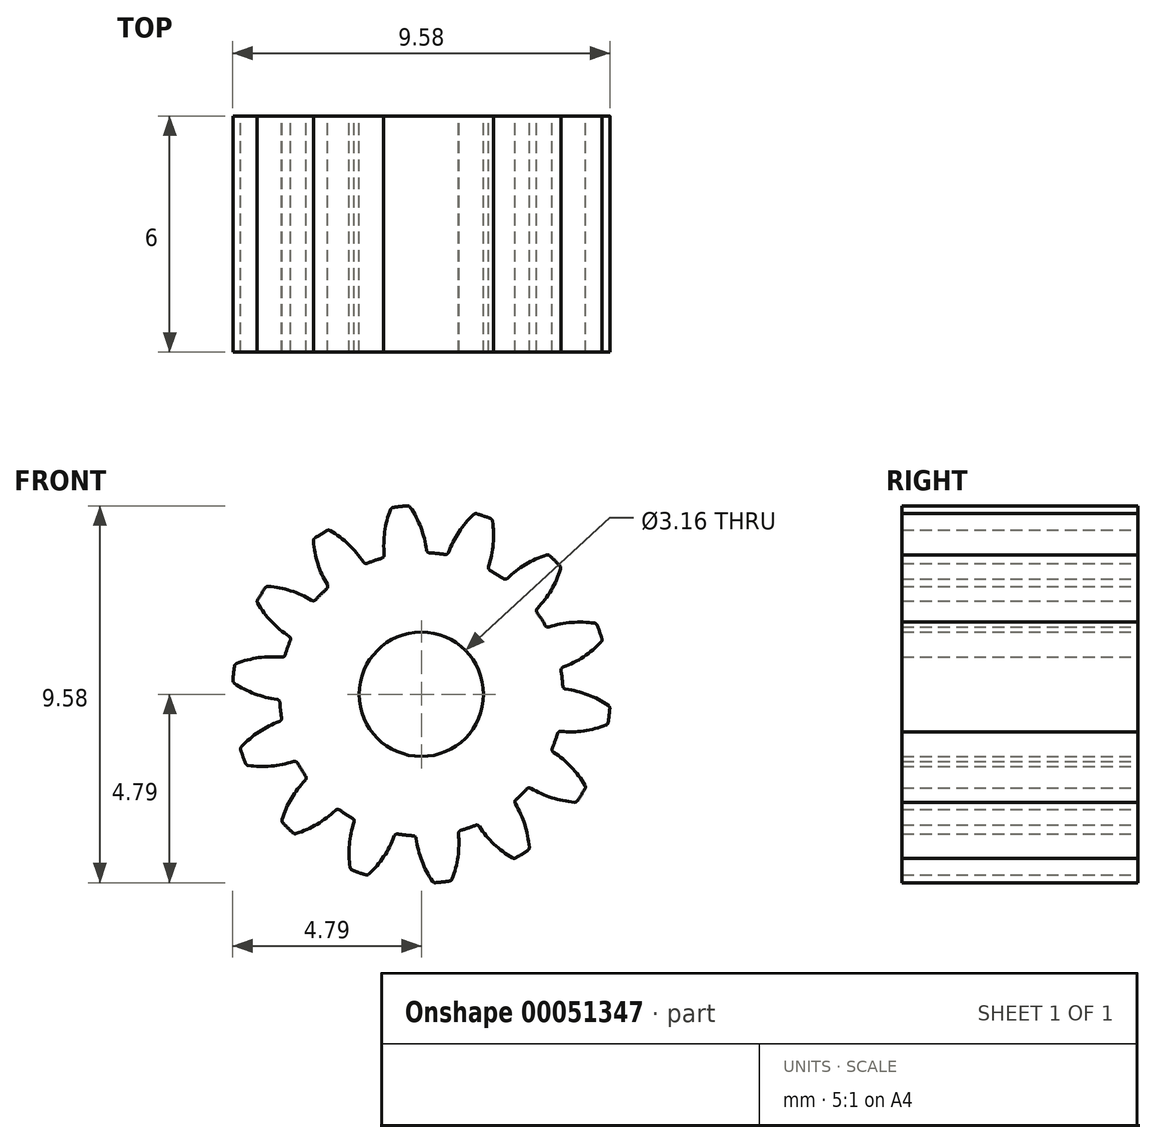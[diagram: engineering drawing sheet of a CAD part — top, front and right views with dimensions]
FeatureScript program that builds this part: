
annotation { "Feature Type Name" : "Feature", "Feature Type Description" : "" }
export const myFeature = defineFeature(function(context is Context, id is Id, definition is map)
    precondition{}
    {
        {
            var Q0;
            Q0=qCreatedBy(makeId("Front.planeOp"),FACE);
            var sketch = newSketch(context, id + "F0", { "sketchPlane" : qUnion([Q0])});
            skCircle(sketch, "E0", {"center": v(0, 0) * mm, "radius": 3.6 * mm, "construction": true});
            skCircle(sketch, "E1", {"center": v(0, 0) * mm, "radius": 4.2 * mm, "construction": true});
            skCircle(sketch, "E2", {"center": v(0, 0) * mm, "radius": 4.8 * mm, "construction": true});
            skLineSegment(sketch, "E3", {"start": v(0, 5.34) * mm, "end": v(0, -5.6) * mm, "construction": true});
            skLineSegment(sketch, "E4", {"start": v(0, 0) * mm, "end": v(-0.7, 6.23) * mm, "construction": true});
            skLineSegment(sketch, "E5", {"start": v(0, 4.2) * mm, "end": v(-5.98, 4.2) * mm, "construction": true});
            skLineSegment(sketch, "E6", {"start": v(0, 4.2) * mm, "end": v(-6, 2.02) * mm, "construction": true});
            skCircle(sketch, "E7", {"center": v(0, 4.2) * mm, "radius": 2.52 * mm, "construction": true});
            skPoint(sketch, "E8", {"position": v(-2.37, 3.34) * mm});
            skCircle(sketch, "E9", {"center": v(-2.37, 3.34) * mm, "radius": 2.52 * mm, "construction": true});
            skArc(sketch, "E10", {"start": v(0.13, 3.67) * mm, "mid": v(-0.01, 4.23) * mm, "end": v(-0.28, 4.75) * mm});
            skArc(sketch, "E11.MirrorCS", {"start": v(-0.94, 3.55) * mm, "mid": v(-0.93, 4.13) * mm, "end": v(-0.78, 4.7) * mm});
            skArc(sketch, "E12", {"start": v(-0.36, 4.79) * mm, "mid": v(-0.54, 4.77) * mm, "end": v(-0.72, 4.75) * mm});
            skArc(sketch, "E13", {"start": v(0.2, 3.6) * mm, "mid": v(0.4, -3.58) * mm, "end": v(-1, 3.46) * mm});
            skPoint(sketch, "E14.visualSharp", {"position": v(-0.94, 3.48) * mm});
            skArc(sketch, "E14.filletArc", {"start": v(-1, 3.46) * mm, "mid": v(-0.96, 3.5) * mm, "end": v(-0.94, 3.55) * mm});
            skPoint(sketch, "E15.visualSharp", {"position": v(0.14, 3.6) * mm});
            skArc(sketch, "E15.filletArc", {"start": v(0.13, 3.67) * mm, "mid": v(0.16, 3.62) * mm, "end": v(0.2, 3.6) * mm});
            skPoint(sketch, "E16.visualSharp", {"position": v(-0.3, 4.8) * mm});
            skArc(sketch, "E16.filletArc", {"start": v(-0.28, 4.75) * mm, "mid": v(-0.31, 4.78) * mm, "end": v(-0.36, 4.79) * mm});
            skPoint(sketch, "E17.visualSharp", {"position": v(-0.77, 4.74) * mm});
            skArc(sketch, "E17.filletArc", {"start": v(-0.72, 4.75) * mm, "mid": v(-0.76, 4.73) * mm, "end": v(-0.78, 4.7) * mm});
            skArc(sketch, "E18.1.0", {"start": v(-2.4, 2.68) * mm, "mid": v(-2.38, 2.73) * mm, "end": v(-2.39, 2.79) * mm});
            skArc(sketch, "E18.1.1", {"start": v(-2.39, 2.79) * mm, "mid": v(-2.63, 3.32) * mm, "end": v(-2.74, 3.89) * mm});
            skArc(sketch, "E18.1.2", {"start": v(-2.7, 3.96) * mm, "mid": v(-2.73, 3.93) * mm, "end": v(-2.74, 3.89) * mm});
            skArc(sketch, "E18.1.3", {"start": v(-2.4, 4.16) * mm, "mid": v(-2.55, 4.06) * mm, "end": v(-2.7, 3.96) * mm});
            skArc(sketch, "E18.1.4", {"start": v(-2.31, 4.16) * mm, "mid": v(-2.36, 4.17) * mm, "end": v(-2.4, 4.16) * mm});
            skArc(sketch, "E18.1.5", {"start": v(-1.47, 3.36) * mm, "mid": v(-1.85, 3.8) * mm, "end": v(-2.31, 4.16) * mm});
            skArc(sketch, "E18.1.6", {"start": v(-1.47, 3.36) * mm, "mid": v(-1.43, 3.33) * mm, "end": v(-1.37, 3.33) * mm});
            skArc(sketch, "E18.2.0", {"start": v(-3.33, 1.37) * mm, "mid": v(-3.33, 1.43) * mm, "end": v(-3.36, 1.47) * mm});
            skArc(sketch, "E18.2.1", {"start": v(-3.36, 1.47) * mm, "mid": v(-3.8, 1.85) * mm, "end": v(-4.16, 2.31) * mm});
            skArc(sketch, "E18.2.2", {"start": v(-4.16, 2.4) * mm, "mid": v(-4.17, 2.36) * mm, "end": v(-4.16, 2.31) * mm});
            skArc(sketch, "E18.2.3", {"start": v(-3.96, 2.7) * mm, "mid": v(-4.06, 2.55) * mm, "end": v(-4.16, 2.4) * mm});
            skArc(sketch, "E18.2.4", {"start": v(-3.89, 2.74) * mm, "mid": v(-3.93, 2.73) * mm, "end": v(-3.96, 2.7) * mm});
            skArc(sketch, "E18.2.5", {"start": v(-2.79, 2.39) * mm, "mid": v(-3.32, 2.63) * mm, "end": v(-3.89, 2.74) * mm});
            skArc(sketch, "E18.2.6", {"start": v(-2.79, 2.39) * mm, "mid": v(-2.73, 2.38) * mm, "end": v(-2.68, 2.4) * mm});
            skArc(sketch, "E18.3.0", {"start": v(-3.6, -0.2) * mm, "mid": v(-3.62, -0.16) * mm, "end": v(-3.67, -0.13) * mm});
            skArc(sketch, "E18.3.1", {"start": v(-3.67, -0.13) * mm, "mid": v(-4.23, 0.01) * mm, "end": v(-4.75, 0.28) * mm});
            skArc(sketch, "E18.3.2", {"start": v(-4.79, 0.36) * mm, "mid": v(-4.78, 0.31) * mm, "end": v(-4.75, 0.28) * mm});
            skArc(sketch, "E18.3.3", {"start": v(-4.75, 0.72) * mm, "mid": v(-4.77, 0.54) * mm, "end": v(-4.79, 0.36) * mm});
            skArc(sketch, "E18.3.4", {"start": v(-4.7, 0.78) * mm, "mid": v(-4.73, 0.76) * mm, "end": v(-4.75, 0.72) * mm});
            skArc(sketch, "E18.3.5", {"start": v(-3.55, 0.94) * mm, "mid": v(-4.13, 0.93) * mm, "end": v(-4.7, 0.78) * mm});
            skArc(sketch, "E18.3.6", {"start": v(-3.55, 0.94) * mm, "mid": v(-3.5, 0.96) * mm, "end": v(-3.46, 1) * mm});
            skArc(sketch, "E18.4.0", {"start": v(-3.15, -1.75) * mm, "mid": v(-3.2, -1.71) * mm, "end": v(-3.25, -1.7) * mm});
            skArc(sketch, "E18.4.1", {"start": v(-3.25, -1.7) * mm, "mid": v(-3.82, -1.83) * mm, "end": v(-4.4, -1.8) * mm});
            skArc(sketch, "E18.4.2", {"start": v(-4.47, -1.76) * mm, "mid": v(-4.44, -1.8) * mm, "end": v(-4.4, -1.8) * mm});
            skArc(sketch, "E18.4.3", {"start": v(-4.59, -1.41) * mm, "mid": v(-4.53, -1.59) * mm, "end": v(-4.47, -1.76) * mm});
            skArc(sketch, "E18.4.4", {"start": v(-4.57, -1.33) * mm, "mid": v(-4.59, -1.37) * mm, "end": v(-4.59, -1.41) * mm});
            skArc(sketch, "E18.4.5", {"start": v(-3.6, -0.69) * mm, "mid": v(-4.12, -0.95) * mm, "end": v(-4.57, -1.33) * mm});
            skArc(sketch, "E18.4.6", {"start": v(-3.6, -0.69) * mm, "mid": v(-3.56, -0.65) * mm, "end": v(-3.55, -0.6) * mm});
            skArc(sketch, "E18.5.0", {"start": v(-2.08, -2.94) * mm, "mid": v(-2.13, -2.92) * mm, "end": v(-2.18, -2.95) * mm});
            skArc(sketch, "E18.5.1", {"start": v(-2.18, -2.95) * mm, "mid": v(-2.65, -3.3) * mm, "end": v(-3.18, -3.54) * mm});
            skArc(sketch, "E18.5.2", {"start": v(-3.26, -3.52) * mm, "mid": v(-3.22, -3.54) * mm, "end": v(-3.18, -3.54) * mm});
            skArc(sketch, "E18.5.3", {"start": v(-3.52, -3.26) * mm, "mid": v(-3.4, -3.4) * mm, "end": v(-3.26, -3.52) * mm});
            skArc(sketch, "E18.5.4", {"start": v(-3.54, -3.18) * mm, "mid": v(-3.54, -3.22) * mm, "end": v(-3.52, -3.26) * mm});
            skArc(sketch, "E18.5.5", {"start": v(-2.95, -2.18) * mm, "mid": v(-3.3, -2.65) * mm, "end": v(-3.54, -3.18) * mm});
            skArc(sketch, "E18.5.6", {"start": v(-2.95, -2.18) * mm, "mid": v(-2.92, -2.13) * mm, "end": v(-2.94, -2.08) * mm});
            skArc(sketch, "E18.6.0", {"start": v(-0.6, -3.55) * mm, "mid": v(-0.65, -3.56) * mm, "end": v(-0.69, -3.6) * mm});
            skArc(sketch, "E18.6.1", {"start": v(-0.69, -3.6) * mm, "mid": v(-0.95, -4.12) * mm, "end": v(-1.33, -4.57) * mm});
            skArc(sketch, "E18.6.2", {"start": v(-1.41, -4.59) * mm, "mid": v(-1.37, -4.59) * mm, "end": v(-1.33, -4.57) * mm});
            skArc(sketch, "E18.6.3", {"start": v(-1.76, -4.47) * mm, "mid": v(-1.59, -4.53) * mm, "end": v(-1.41, -4.59) * mm});
            skArc(sketch, "E18.6.4", {"start": v(-1.8, -4.4) * mm, "mid": v(-1.8, -4.44) * mm, "end": v(-1.76, -4.47) * mm});
            skArc(sketch, "E18.6.5", {"start": v(-1.7, -3.25) * mm, "mid": v(-1.83, -3.82) * mm, "end": v(-1.8, -4.4) * mm});
            skArc(sketch, "E18.6.6", {"start": v(-1.7, -3.25) * mm, "mid": v(-1.71, -3.2) * mm, "end": v(-1.75, -3.15) * mm});
            skArc(sketch, "E18.7.0", {"start": v(1, -3.46) * mm, "mid": v(0.96, -3.5) * mm, "end": v(0.94, -3.55) * mm});
            skArc(sketch, "E18.7.1", {"start": v(0.94, -3.55) * mm, "mid": v(0.93, -4.13) * mm, "end": v(0.78, -4.7) * mm});
            skArc(sketch, "E18.7.2", {"start": v(0.72, -4.75) * mm, "mid": v(0.76, -4.73) * mm, "end": v(0.78, -4.7) * mm});
            skArc(sketch, "E18.7.3", {"start": v(0.36, -4.79) * mm, "mid": v(0.54, -4.77) * mm, "end": v(0.72, -4.75) * mm});
            skArc(sketch, "E18.7.4", {"start": v(0.28, -4.75) * mm, "mid": v(0.31, -4.78) * mm, "end": v(0.36, -4.79) * mm});
            skArc(sketch, "E18.7.5", {"start": v(-0.13, -3.67) * mm, "mid": v(0.01, -4.23) * mm, "end": v(0.28, -4.75) * mm});
            skArc(sketch, "E18.7.6", {"start": v(-0.13, -3.67) * mm, "mid": v(-0.16, -3.62) * mm, "end": v(-0.2, -3.6) * mm});
            skArc(sketch, "E18.8.0", {"start": v(2.4, -2.68) * mm, "mid": v(2.38, -2.73) * mm, "end": v(2.39, -2.79) * mm});
            skArc(sketch, "E18.8.1", {"start": v(2.39, -2.79) * mm, "mid": v(2.63, -3.32) * mm, "end": v(2.74, -3.89) * mm});
            skArc(sketch, "E18.8.2", {"start": v(2.7, -3.96) * mm, "mid": v(2.73, -3.93) * mm, "end": v(2.74, -3.89) * mm});
            skArc(sketch, "E18.8.3", {"start": v(2.4, -4.16) * mm, "mid": v(2.55, -4.06) * mm, "end": v(2.7, -3.96) * mm});
            skArc(sketch, "E18.8.4", {"start": v(2.31, -4.16) * mm, "mid": v(2.36, -4.17) * mm, "end": v(2.4, -4.16) * mm});
            skArc(sketch, "E18.8.5", {"start": v(1.47, -3.36) * mm, "mid": v(1.85, -3.8) * mm, "end": v(2.31, -4.16) * mm});
            skArc(sketch, "E18.8.6", {"start": v(1.47, -3.36) * mm, "mid": v(1.43, -3.33) * mm, "end": v(1.37, -3.33) * mm});
            skArc(sketch, "E18.9.0", {"start": v(3.33, -1.37) * mm, "mid": v(3.33, -1.43) * mm, "end": v(3.36, -1.47) * mm});
            skArc(sketch, "E18.9.1", {"start": v(3.36, -1.47) * mm, "mid": v(3.8, -1.85) * mm, "end": v(4.16, -2.31) * mm});
            skArc(sketch, "E18.9.2", {"start": v(4.16, -2.4) * mm, "mid": v(4.17, -2.36) * mm, "end": v(4.16, -2.31) * mm});
            skArc(sketch, "E18.9.3", {"start": v(3.96, -2.7) * mm, "mid": v(4.06, -2.55) * mm, "end": v(4.16, -2.4) * mm});
            skArc(sketch, "E18.9.4", {"start": v(3.89, -2.74) * mm, "mid": v(3.93, -2.73) * mm, "end": v(3.96, -2.7) * mm});
            skArc(sketch, "E18.9.5", {"start": v(2.79, -2.39) * mm, "mid": v(3.32, -2.63) * mm, "end": v(3.89, -2.74) * mm});
            skArc(sketch, "E18.9.6", {"start": v(2.79, -2.39) * mm, "mid": v(2.73, -2.38) * mm, "end": v(2.68, -2.4) * mm});
            skArc(sketch, "E18.10.0", {"start": v(3.6, 0.2) * mm, "mid": v(3.62, 0.16) * mm, "end": v(3.67, 0.13) * mm});
            skArc(sketch, "E18.10.1", {"start": v(3.67, 0.13) * mm, "mid": v(4.23, -0.01) * mm, "end": v(4.75, -0.28) * mm});
            skArc(sketch, "E18.10.2", {"start": v(4.79, -0.36) * mm, "mid": v(4.78, -0.31) * mm, "end": v(4.75, -0.28) * mm});
            skArc(sketch, "E18.10.3", {"start": v(4.75, -0.72) * mm, "mid": v(4.77, -0.54) * mm, "end": v(4.79, -0.36) * mm});
            skArc(sketch, "E18.10.4", {"start": v(4.7, -0.78) * mm, "mid": v(4.73, -0.76) * mm, "end": v(4.75, -0.72) * mm});
            skArc(sketch, "E18.10.5", {"start": v(3.55, -0.94) * mm, "mid": v(4.13, -0.93) * mm, "end": v(4.7, -0.78) * mm});
            skArc(sketch, "E18.10.6", {"start": v(3.55, -0.94) * mm, "mid": v(3.5, -0.96) * mm, "end": v(3.46, -1) * mm});
            skArc(sketch, "E18.11.0", {"start": v(3.15, 1.75) * mm, "mid": v(3.2, 1.71) * mm, "end": v(3.25, 1.7) * mm});
            skArc(sketch, "E18.11.1", {"start": v(3.25, 1.7) * mm, "mid": v(3.82, 1.83) * mm, "end": v(4.4, 1.8) * mm});
            skArc(sketch, "E18.11.2", {"start": v(4.47, 1.76) * mm, "mid": v(4.44, 1.8) * mm, "end": v(4.4, 1.8) * mm});
            skArc(sketch, "E18.11.3", {"start": v(4.59, 1.41) * mm, "mid": v(4.53, 1.59) * mm, "end": v(4.47, 1.76) * mm});
            skArc(sketch, "E18.11.4", {"start": v(4.57, 1.33) * mm, "mid": v(4.59, 1.37) * mm, "end": v(4.59, 1.41) * mm});
            skArc(sketch, "E18.11.5", {"start": v(3.6, 0.69) * mm, "mid": v(4.12, 0.95) * mm, "end": v(4.57, 1.33) * mm});
            skArc(sketch, "E18.11.6", {"start": v(3.6, 0.69) * mm, "mid": v(3.56, 0.65) * mm, "end": v(3.55, 0.6) * mm});
            skArc(sketch, "E18.12.0", {"start": v(2.08, 2.94) * mm, "mid": v(2.13, 2.92) * mm, "end": v(2.18, 2.95) * mm});
            skArc(sketch, "E18.12.1", {"start": v(2.18, 2.95) * mm, "mid": v(2.65, 3.3) * mm, "end": v(3.18, 3.54) * mm});
            skArc(sketch, "E18.12.2", {"start": v(3.26, 3.52) * mm, "mid": v(3.22, 3.54) * mm, "end": v(3.18, 3.54) * mm});
            skArc(sketch, "E18.12.3", {"start": v(3.52, 3.26) * mm, "mid": v(3.4, 3.4) * mm, "end": v(3.26, 3.52) * mm});
            skArc(sketch, "E18.12.4", {"start": v(3.54, 3.18) * mm, "mid": v(3.54, 3.22) * mm, "end": v(3.52, 3.26) * mm});
            skArc(sketch, "E18.12.5", {"start": v(2.95, 2.18) * mm, "mid": v(3.3, 2.65) * mm, "end": v(3.54, 3.18) * mm});
            skArc(sketch, "E18.12.6", {"start": v(2.95, 2.18) * mm, "mid": v(2.92, 2.13) * mm, "end": v(2.94, 2.08) * mm});
            skArc(sketch, "E18.13.0", {"start": v(0.6, 3.55) * mm, "mid": v(0.65, 3.56) * mm, "end": v(0.69, 3.6) * mm});
            skArc(sketch, "E18.13.1", {"start": v(0.69, 3.6) * mm, "mid": v(0.95, 4.12) * mm, "end": v(1.33, 4.57) * mm});
            skArc(sketch, "E18.13.2", {"start": v(1.41, 4.59) * mm, "mid": v(1.37, 4.59) * mm, "end": v(1.33, 4.57) * mm});
            skArc(sketch, "E18.13.3", {"start": v(1.76, 4.47) * mm, "mid": v(1.59, 4.53) * mm, "end": v(1.41, 4.59) * mm});
            skArc(sketch, "E18.13.4", {"start": v(1.8, 4.4) * mm, "mid": v(1.8, 4.44) * mm, "end": v(1.76, 4.47) * mm});
            skArc(sketch, "E18.13.5", {"start": v(1.7, 3.25) * mm, "mid": v(1.83, 3.82) * mm, "end": v(1.8, 4.4) * mm});
            skArc(sketch, "E18.13.6", {"start": v(1.7, 3.25) * mm, "mid": v(1.71, 3.2) * mm, "end": v(1.75, 3.15) * mm});
            skCircle(sketch, "E19", {"center": v(0, 0) * mm, "radius": 1.58 * mm});
            skSolve(sketch);
        }
        {
            var Q0;
            Q0 = qSketchRegion(id + "F0", true);
            extrude(context, id + "F1", {"entities" : qUnion([Q0]), "depth" : 6 * mm, "symmetric" : true});
        }
    });
